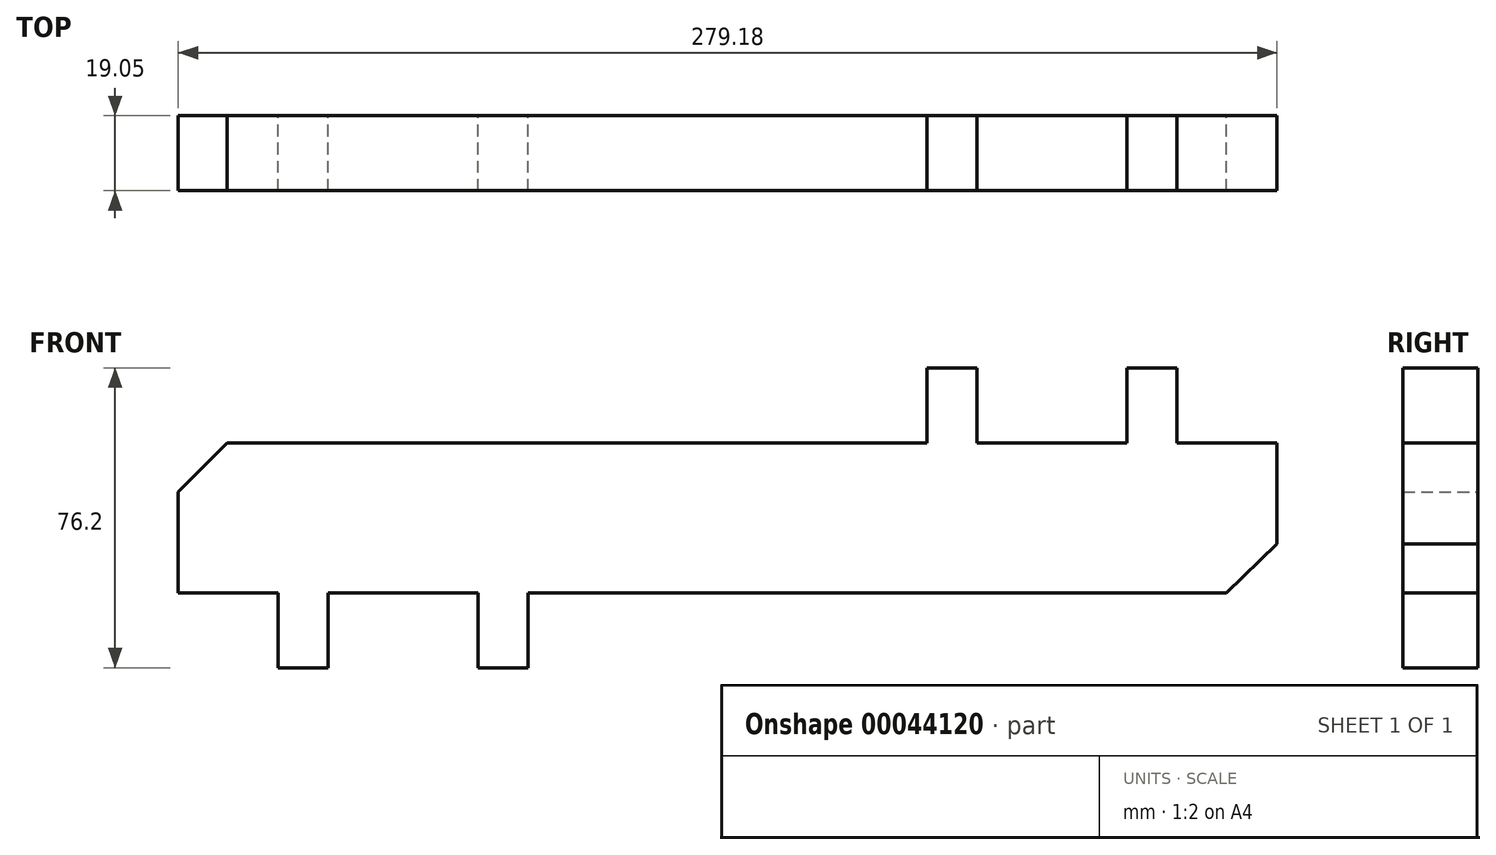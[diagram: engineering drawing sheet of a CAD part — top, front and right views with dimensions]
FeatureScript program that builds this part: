
annotation { "Feature Type Name" : "Feature", "Feature Type Description" : "" }
export const myFeature = defineFeature(function(context is Context, id is Id, definition is map)
    precondition{}
    {
        {
            var Q0;
            Q0=qCreatedBy(makeId("Front.planeOp"),FACE);
            var sketch = newSketch(context, id + "F0", { "sketchPlane" : qUnion([Q0])});
            skPoint(sketch, "E0.rect.middle", {"position": v(0, 0) * mm});
            skLineSegment(sketch, "E1", {"start": v(-115.11, -17.36) * mm, "end": v(-115.11, -36.4) * mm});
            skLineSegment(sketch, "E2", {"start": v(-115.11, -36.4) * mm, "end": v(-102.41, -36.4) * mm});
            skLineSegment(sketch, "E3", {"start": v(-102.41, -36.4) * mm, "end": v(-102.41, -17.36) * mm});
            skLineSegment(sketch, "E4", {"start": v(-64.31, -17.36) * mm, "end": v(-64.31, -36.4) * mm});
            skLineSegment(sketch, "E5", {"start": v(-64.31, -36.4) * mm, "end": v(-51.61, -36.4) * mm});
            skLineSegment(sketch, "E6", {"start": v(-51.61, -36.4) * mm, "end": v(-51.61, -17.36) * mm});
            skLineSegment(sketch, "E7", {"start": v(100.56, 20.74) * mm, "end": v(100.56, 39.8) * mm});
            skLineSegment(sketch, "E8", {"start": v(113.26, 39.8) * mm, "end": v(100.56, 39.8) * mm});
            skLineSegment(sketch, "E9", {"start": v(113.26, 39.8) * mm, "end": v(113.26, 20.74) * mm});
            skLineSegment(sketch, "E10", {"start": v(49.76, 20.74) * mm, "end": v(49.76, 39.8) * mm});
            skLineSegment(sketch, "E11", {"start": v(62.46, 39.8) * mm, "end": v(49.76, 39.8) * mm});
            skLineSegment(sketch, "E12", {"start": v(62.46, 39.8) * mm, "end": v(62.46, 20.74) * mm});
            skLineSegment(sketch, "E13", {"start": v(-140.52, 8.26) * mm, "end": v(-128.04, 20.74) * mm});
            skLineSegment(sketch, "E14", {"start": v(125.73, -17.36) * mm, "end": v(138.66, -4.89) * mm});
            skLineSegment(sketch, "E15", {"start": v(-140.52, -17.36) * mm, "end": v(-140.52, 8.26) * mm});
            skLineSegment(sketch, "E16", {"start": v(138.66, 20.74) * mm, "end": v(138.66, -4.89) * mm});
            skLineSegment(sketch, "E17", {"start": v(-140.52, -17.36) * mm, "end": v(-115.11, -17.36) * mm});
            skLineSegment(sketch, "E18", {"start": v(-128.04, 20.74) * mm, "end": v(49.76, 20.74) * mm});
            skLineSegment(sketch, "E19.trimOffspring", {"start": v(62.46, 20.74) * mm, "end": v(100.56, 20.74) * mm});
            skLineSegment(sketch, "E20.trimOffspring", {"start": v(113.26, 20.74) * mm, "end": v(138.66, 20.74) * mm});
            skLineSegment(sketch, "E21.trimOffspring", {"start": v(-51.61, -17.36) * mm, "end": v(125.73, -17.36) * mm});
            skLineSegment(sketch, "E22.trimOffspring", {"start": v(-102.41, -17.36) * mm, "end": v(-64.31, -17.36) * mm});
            skSolve(sketch);
        }
        {
            var Q0;
            Q0=makeQuery(id+"F0.imprint","IMPRINT",FACE,{"disambiguationData":[TD([[makeQuery(id+"F0.imprint","IMPRINT",EDGE,{"derivedFrom":sQuery(id+"F0.wireOp",EDGE,"E0.rect.bottom")}),1.0]])]});
            var Q1;
            {var subQ0=sQuery(id+"F0.wireOp",EDGE,"E10");Q1=makeQuery(id+"F0.imprint","IMPRINT",FACE,{"disambiguationData":[TD([[makeQuery(id+"F0.imprint","IMPRINT",EDGE,{"derivedFrom":subQ0}),-1.0]])]});}
            var Q2;
            {var subQ0=sQuery(id+"F0.wireOp",EDGE,"E7");Q2=makeQuery(id+"F0.imprint","IMPRINT",FACE,{"disambiguationData":[TD([[makeQuery(id+"F0.imprint","IMPRINT",EDGE,{"derivedFrom":subQ0}),-1.0]])]});}
            var Q3;
            {var subQ0=sQuery(id+"F0.wireOp",EDGE,"E4");Q3=makeQuery(id+"F0.imprint","IMPRINT",FACE,{"disambiguationData":[TD([[makeQuery(id+"F0.imprint","IMPRINT",EDGE,{"derivedFrom":subQ0}),1.0]])]});}
            var Q4;
            {var subQ0=sQuery(id+"F0.wireOp",EDGE,"E1");Q4=makeQuery(id+"F0.imprint","IMPRINT",FACE,{"disambiguationData":[TD([[makeQuery(id+"F0.imprint","IMPRINT",EDGE,{"derivedFrom":subQ0}),1.0]])]});}
            extrude(context, id + "F1", {"entities" : qUnion([Q0, Q1, Q2, Q3, Q4]), "depth" : 19.05 * mm});
        }
    });
